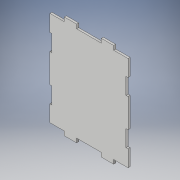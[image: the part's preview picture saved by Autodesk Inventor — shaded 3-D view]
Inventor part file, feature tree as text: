
AUTODESK INVENTOR PART (.ipt)
format: ipt  version: 2017 (Build 210142000, 142)  size: 163,328 bytes
history: native  units: in
note: dims shown in document units (in); Inventor stores cm internally (conversion verified against a paired STEP export)
features: extrude x3, sketch x3, plane x2, mirror x2, projected_geometry x2
ambient origin geometry x8: Origin, YZ Plane, XZ Plane, XY Plane, X Axis, Y Axis, Z Axis, Center Point
bodies: Solid1 (feature_tree)
feature tree (12):
  extrude  "Extrusion1"  Depth=46.0in
  extrude  "Extrusion2"  Depth=6.0in
  extrude  "Extrusion3"  Depth=2.0in TaperAngle=0.0deg
  plane  "Work Plane1"
  mirror  "Mirror1"
  plane  "Work Plane2"
  mirror  "Mirror2"
  sketch  "Sketch1"  dims[d0=38.0in d1=46.0in]
  sketch  "Sketch2"  dims[d2=1.0in d3=0.0in d4=6.0in]
  projected_geometry  "Projected Loop1"
  sketch  "Sketch3"  dims[d5=7.0in d6=2.0in d7=0.0in d8=8.0in d9=8.0in d10=1.0in d11=0.0in d12=14.0in d13=8.0in]
  projected_geometry  "Projected Loop2"
